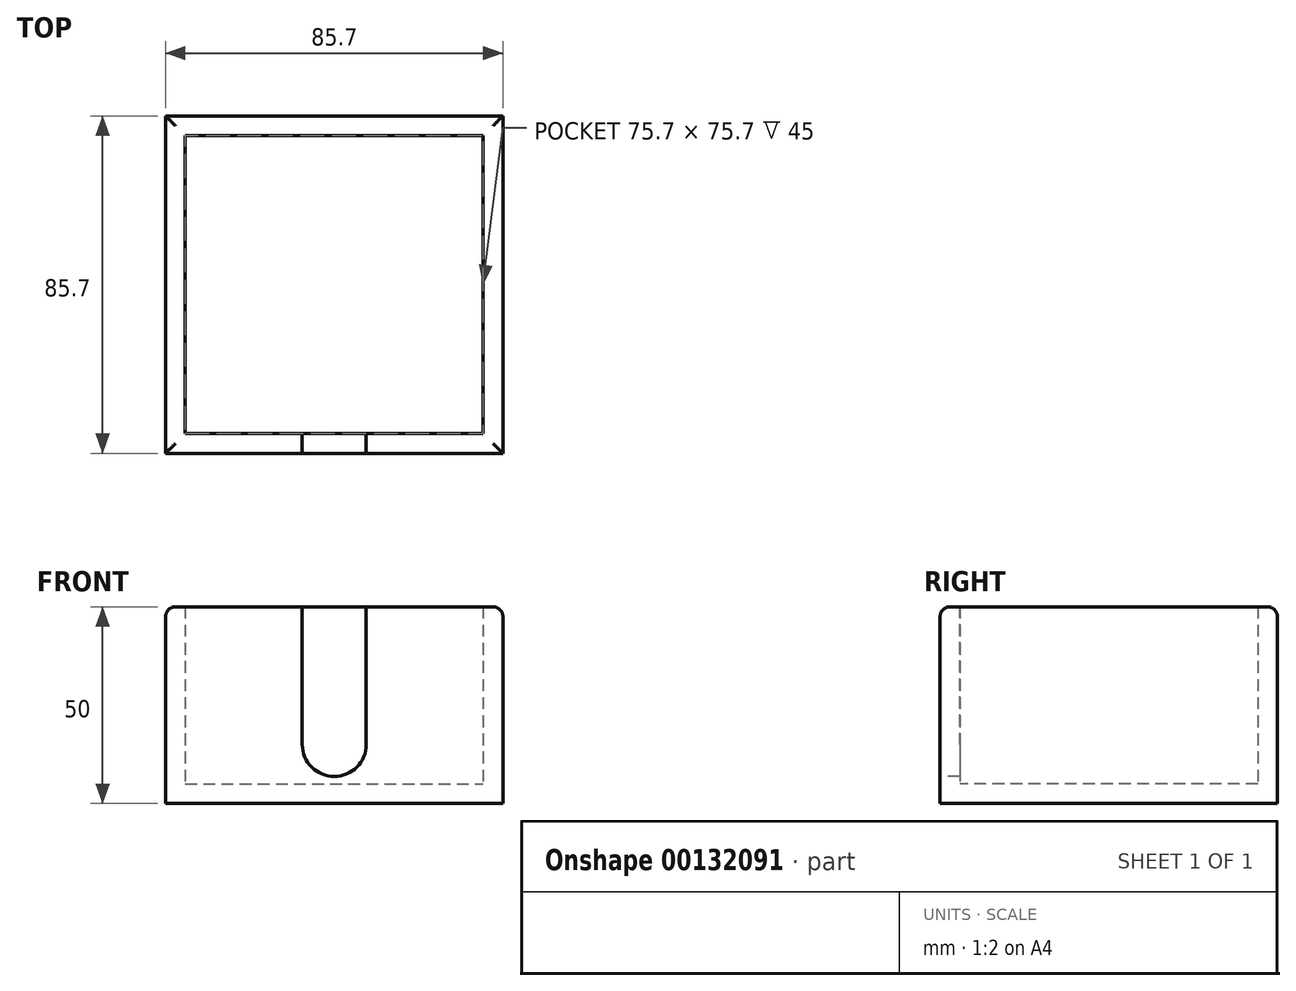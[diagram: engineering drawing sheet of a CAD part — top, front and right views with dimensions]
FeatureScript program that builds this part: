
annotation { "Feature Type Name" : "Feature", "Feature Type Description" : "" }
export const myFeature = defineFeature(function(context is Context, id is Id, definition is map)
    precondition{}
    {
        {
            var Q0;
            Q0=qCreatedBy(makeId("Top.planeOp"),FACE);
            var sketch = newSketch(context, id + "F0", { "sketchPlane" : qUnion([Q0])});
            skLineSegment(sketch, "E0.bottom", {"start": v(-37.85, 37.85) * mm, "end": v(37.85, 37.85) * mm});
            skLineSegment(sketch, "E0.top", {"start": v(-37.85, -37.85) * mm, "end": v(37.85, -37.85) * mm});
            skLineSegment(sketch, "E0.left", {"start": v(-37.85, 37.85) * mm, "end": v(-37.85, -37.85) * mm});
            skLineSegment(sketch, "E0.right", {"start": v(37.85, 37.85) * mm, "end": v(37.85, -37.85) * mm});
            skPoint(sketch, "E0.middle", {"position": v(0, 0) * mm});
            skLineSegment(sketch, "E1.0", {"start": v(-42.85, 42.85) * mm, "end": v(-42.85, -42.85) * mm});
            skLineSegment(sketch, "E1.1", {"start": v(-42.85, 42.85) * mm, "end": v(42.85, 42.85) * mm});
            skLineSegment(sketch, "E1.2", {"start": v(42.85, 42.85) * mm, "end": v(42.85, -42.85) * mm});
            skLineSegment(sketch, "E1.3", {"start": v(-42.85, -42.85) * mm, "end": v(42.85, -42.85) * mm});
            skSolve(sketch);
        }
        {
            var Q0;
            Q0=makeQuery(id+"F0.imprint","IMPRINT",FACE,{"disambiguationData":[TD([[makeQuery(id+"F0.imprint","IMPRINT",EDGE,{"derivedFrom":sQuery(id+"F0.wireOp",EDGE,"E0.bottom")}),1.0]])]});
            extrude(context, id + "F1", {"entities" : qUnion([Q0]), "depth" : 50 * mm});
        }
        {
            var Q0;
            Q0=makeQuery(id+"F0.imprint","IMPRINT",FACE,{"disambiguationData":[TD([[makeQuery(id+"F0.imprint","IMPRINT",EDGE,{"derivedFrom":sQuery(id+"F0.wireOp",EDGE,"E0.bottom")}),-1.0]])]});
            extrude(context, id + "F2", {"entities" : qUnion([Q0]), "operationType" : NewBodyOperationType.ADD, "depth" : 5 * mm});
        }
        {
            var Q0;
            Q0=makeQuery(id+"F1.opExtrude","SWEPT_FACE",FACE,{"disambiguationData":[OSD([sQuery(id+"F0.wireOp",EDGE,"E1.3")])]});
            var sketch = newSketch(context, id + "F3", { "sketchPlane" : qUnion([Q0])});
            skLineSegment(sketch, "E2.0", {"start": v(8.12, 50) * mm, "end": v(8.12, 15) * mm});
            skLineSegment(sketch, "E3.0", {"start": v(-49.2, -6.35) * mm, "end": v(49.2, -6.35) * mm});
            skLineSegment(sketch, "E3.1", {"start": v(-49.2, 56.35) * mm, "end": v(-49.2, -6.35) * mm});
            skLineSegment(sketch, "E3.2", {"start": v(49.2, 56.35) * mm, "end": v(-49.2, 56.35) * mm});
            skLineSegment(sketch, "E3.3", {"start": v(49.2, -6.35) * mm, "end": v(49.2, 56.35) * mm});
            skLineSegment(sketch, "E4.MirrorCS", {"start": v(-8.12, 50) * mm, "end": v(-8.12, 15) * mm});
            skLineSegment(sketch, "E5", {"start": v(8.12, 15) * mm, "end": v(-8.12, 15) * mm});
            skCircle(sketch, "E6", {"center": v(0, 15) * mm, "radius": 8.12 * mm});
            skSolve(sketch);
        }
        {
            var Q0;
            {var subQ0=sQuery(id+"F3.wireOp",EDGE,"E5");Q0=makeQuery(id+"F3.imprint","IMPRINT",FACE,{"disambiguationData":[TD([[makeQuery(id+"F3.imprint","IMPRINT",EDGE,{"derivedFrom":subQ0}),1.0]])]});}
            var Q1;
            {var subQ0=sQuery(id+"F3.wireOp",EDGE,"E5");Q1=makeQuery(id+"F3.imprint","IMPRINT",FACE,{"disambiguationData":[TD([[makeQuery(id+"F3.imprint","IMPRINT",EDGE,{"derivedFrom":subQ0}),-1.0]])]});}
            var Q2;
            {var subQ0=sQuery(id+"F3.wireOp",EDGE,"E2.0");Q2=makeQuery(id+"F3.imprint","IMPRINT",FACE,{"disambiguationData":[TD([[makeQuery(id+"F3.imprint","IMPRINT",EDGE,{"derivedFrom":subQ0}),-1.0]])]});}
            extrude(context, id + "F4", {"entities" : qUnion([Q0, Q1, Q2]), "operationType" : NewBodyOperationType.REMOVE, "oppositeDirection" : true, "depth" : 20 * mm});
        }
        {
            var Q0;
            Q0=makeQuery(id+"F4.boolean.opBoolean","COPY",EDGE,{"derivedFrom":makeQuery(id+"F4.opExtrude","CAP_EDGE",EDGE,{"disambiguationData":[OSD([sQuery(id+"F3.wireOp",EDGE,"E6")])],"isStart":true})});
            var Q1;
            Q1=makeQuery(id+"F4.boolean.opBoolean","COPY",EDGE,{"derivedFrom":makeQuery(id+"F4.opExtrude","CAP_EDGE",EDGE,{"disambiguationData":[OSD([sQuery(id+"F3.wireOp",EDGE,"E2.0")])],"isStart":true})});
            var Q2;
            {var subQ0=sQuery(id+"F0.wireOp",EDGE,"E1.3");var subQ1=sQuery(id+"F0.wireOp",EDGE,"E1.2");Q2=makeQuery(id+"F4.boolean.opBoolean","SPLIT",EDGE,{"disambiguationData":[TD([makeQuery(id+"F1.opExtrude","SWEPT_FACE",FACE,{"disambiguationData":[OSD([subQ1])]})])],"derivedFrom":makeQuery(id+"F1.opExtrude","CAP_EDGE",EDGE,{"disambiguationData":[OSD([subQ0])],"isStart":false})});}
            var Q3;
            Q3=makeQuery(id+"F1.opExtrude","CAP_EDGE",EDGE,{"disambiguationData":[OSD([sQuery(id+"F0.wireOp",EDGE,"E1.2")])],"isStart":false});
            var Q4;
            Q4=makeQuery(id+"F1.opExtrude","CAP_EDGE",EDGE,{"disambiguationData":[OSD([sQuery(id+"F0.wireOp",EDGE,"E1.1")])],"isStart":false});
            var Q5;
            Q5=makeQuery(id+"F1.opExtrude","CAP_EDGE",EDGE,{"disambiguationData":[OSD([sQuery(id+"F0.wireOp",EDGE,"E1.0")])],"isStart":false});
            var Q6;
            {var subQ0=sQuery(id+"F0.wireOp",EDGE,"E1.3");var subQ1=sQuery(id+"F0.wireOp",EDGE,"E1.0");Q6=makeQuery(id+"F4.boolean.opBoolean","SPLIT",EDGE,{"disambiguationData":[TD([makeQuery(id+"F1.opExtrude","SWEPT_FACE",FACE,{"disambiguationData":[OSD([subQ1])]})])],"derivedFrom":makeQuery(id+"F1.opExtrude","CAP_EDGE",EDGE,{"disambiguationData":[OSD([subQ0])],"isStart":false})});}
            var Q7;
            Q7=makeQuery(id+"F4.boolean.opBoolean","COPY",EDGE,{"derivedFrom":makeQuery(id+"F4.opExtrude","CAP_EDGE",EDGE,{"disambiguationData":[OSD([sQuery(id+"F3.wireOp",EDGE,"E4.MirrorCS")])],"isStart":true})});
            fillet(context, id + "F5", {"entities" : qUnion([Q0, Q1, Q2, Q3, Q4, Q5, Q6, Q7]), "radius" : 2.54 * mm, "tangentPropagation" : true, "allowEdgeOverflow" : false});
        }
    });
